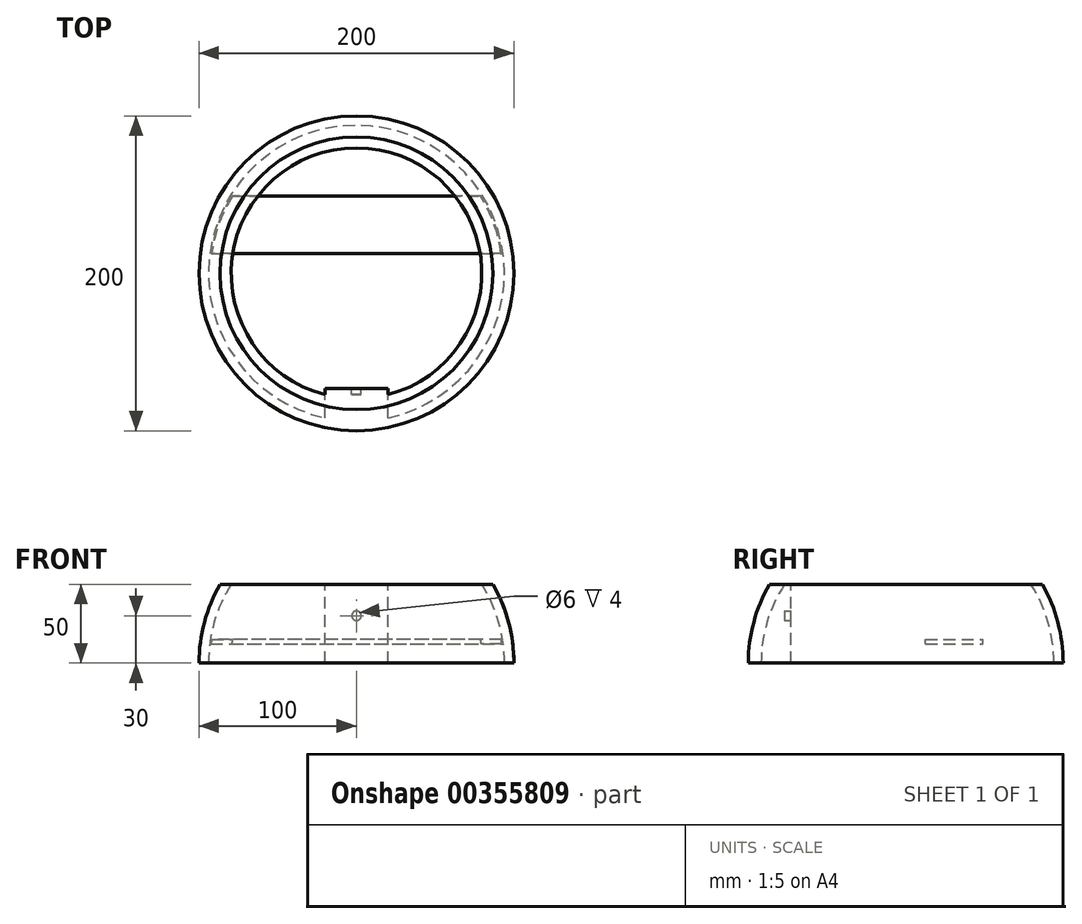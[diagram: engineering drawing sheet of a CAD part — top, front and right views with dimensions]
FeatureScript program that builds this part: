
annotation { "Feature Type Name" : "Feature", "Feature Type Description" : "" }
export const myFeature = defineFeature(function(context is Context, id is Id, definition is map)
    precondition{}
    {
        {
            var Q0;
            Q0=qCreatedBy(makeId("Front.planeOp"),FACE);
            var sketch = newSketch(context, id + "F0", { "sketchPlane" : qUnion([Q0])});
            skArc(sketch, "E0", {"start": v(-86.6, 50) * mm, "mid": v(-96.6, 25.88) * mm, "end": v(-100, 0) * mm});
            skLineSegment(sketch, "E1", {"start": v(0, 50) * mm, "end": v(0, 0) * mm});
            skLineSegment(sketch, "E2", {"start": v(0, 50) * mm, "end": v(-86.6, 50) * mm});
            skLineSegment(sketch, "E3", {"start": v(0, 0) * mm, "end": v(-100, 0) * mm});
            skPoint(sketch, "E4.orphan", {"position": v(0, 100) * mm});
            skSolve(sketch);
        }
        {
            var Q0;
            Q0=qSketchRegion(id+"F0",true);
            var Q1;
            Q1=sQuery(id+"F0.wireOp",EDGE,"E1");
            revolve(context, id + "F1", {"entities" : qUnion([Q0]), "axis" : qUnion([Q1]), "revolveType" : RevolveType.FULL});
        }
        {
            var Q0;
            Q0=makeQuery(id+"F1.opRevolve","SWEPT_FACE",FACE,{"disambiguationData":[OSD([sQuery(id+"F0.wireOp",EDGE,"E2")])]});
            var Q1;
            Q1=makeQuery(id+"F1.opRevolve","SWEPT_FACE",FACE,{"disambiguationData":[OSD([sQuery(id+"F0.wireOp",EDGE,"E3")])]});
            shell(context, id + "F2", {"entities" : qUnion([Q0, Q1]), "thickness" : 6 * mm});
        }
        {
            var Q0;
            Q0=qCreatedBy(makeId("Front.planeOp"),FACE);
            cPlane(context, id + "F3", {"entities" : qUnion([Q0]), "cplaneType" : CPlaneType.OFFSET, "offset" : 49 * mm, "oppositeDirection" : true, "width" : 150 * mm, "height" : 150 * mm});
        }
        {
            var Q0;
            Q0=qCreatedBy(id+"F3.planeOp",FACE);
            var sketch = newSketch(context, id + "F4", { "sketchPlane" : qUnion([Q0])});
            skLineSegment(sketch, "E5", {"start": v(47.2, 15) * mm, "end": v(-12.8, 15) * mm});
            skLineSegment(sketch, "E6", {"start": v(-12.8, 15) * mm, "end": v(-12.8, 12) * mm});
            skLineSegment(sketch, "E7", {"start": v(-12.8, 12) * mm, "end": v(47.2, 12) * mm});
            skLineSegment(sketch, "E8", {"start": v(47.2, 12) * mm, "end": v(47.2, 15) * mm});
            skSolve(sketch);
        }
        {
            var Q0;
            Q0=qSketchRegion(id+"F4",true);
            extrude(context, id + "F5", {"entities" : qUnion([Q0]), "depth" : 36.5 * mm});
        }
        {
            var Q0;
            Q0=makeQuery(id+"F5.opExtrude","SWEPT_FACE",FACE,{"disambiguationData":[OSD([sQuery(id+"F4.wireOp",EDGE,"E8")])]});
            extrude(context, id + "F6", {"entities" : qUnion([Q0]), "operationType" : NewBodyOperationType.ADD, "endBound" : BoundingType.UP_TO_NEXT, "depth" : 25 * mm});
        }
        {
            var Q0;
            Q0=makeQuery(id+"F5.opExtrude","SWEPT_FACE",FACE,{"disambiguationData":[OSD([sQuery(id+"F4.wireOp",EDGE,"E6")])]});
            extrude(context, id + "F7", {"entities" : qUnion([Q0]), "operationType" : NewBodyOperationType.ADD, "endBound" : BoundingType.UP_TO_NEXT, "depth" : 25 * mm});
        }
        {
            var Q0;
            Q0=qCreatedBy(makeId("Front.planeOp"),FACE);
            cPlane(context, id + "F8", {"entities" : qUnion([Q0]), "cplaneType" : CPlaneType.OFFSET, "offset" : 62 * mm, "width" : 150 * mm, "height" : 150 * mm});
        }
        {
            var Q0;
            Q0=qCreatedBy(id+"F8.planeOp",FACE);
            var sketch = newSketch(context, id + "F9", { "sketchPlane" : qUnion([Q0])});
            skLineSegment(sketch, "E9", {"start": v(20, 0) * mm, "end": v(20, 50) * mm});
            skLineSegment(sketch, "E10", {"start": v(-20, 0) * mm, "end": v(-20, 50) * mm});
            skLineSegment(sketch, "E11.0", {"start": v(-20, 0) * mm, "end": v(20, 0) * mm});
            skLineSegment(sketch, "E12.0", {"start": v(-20, 50) * mm, "end": v(20, 50) * mm});
            skPoint(sketch, "E13.orphan", {"position": v(-100, 0) * mm});
            skPoint(sketch, "E14.orphan", {"position": v(-86.6, 50) * mm});
            skPoint(sketch, "E15.orphan", {"position": v(100, 0) * mm});
            skPoint(sketch, "E16.orphan", {"position": v(86.6, 50) * mm});
            skSolve(sketch);
        }
        {
            var Q0;
            Q0=qSketchRegion(id+"F9",true);
            extrude(context, id + "F10", {"entities" : qUnion([Q0]), "operationType" : NewBodyOperationType.ADD, "endBound" : BoundingType.UP_TO_NEXT, "depth" : 25 * mm});
        }
        {
            var Q0;
            Q0=makeQuery(id+"F10.opExtrude","CAP_FACE",FACE,{"disambiguationData":[OSD([sQuery(id+"F9.wireOp",EDGE,"E9"),sQuery(id+"F9.wireOp",EDGE,"E10"),sQuery(id+"F9.wireOp",EDGE,"E11.0"),sQuery(id+"F9.wireOp",EDGE,"E12.0")])],"isStart":true});
            var sketch = newSketch(context, id + "F11", { "sketchPlane" : qUnion([Q0])});
            skCircle(sketch, "E17", {"center": v(0, 30) * mm, "radius": 3 * mm});
            skSolve(sketch);
        }
        {
            var Q0;
            Q0=makeQuery(id+"F11.imprint","IMPRINT",FACE,{"disambiguationData":[TD([[makeQuery(id+"F11.imprint","IMPRINT",EDGE,{"derivedFrom":sQuery(id+"F11.wireOp",EDGE,"E17")}),1.0]])]});
            extrude(context, id + "F12", {"entities" : qUnion([Q0]), "operationType" : NewBodyOperationType.REMOVE, "oppositeDirection" : true, "depth" : 4 * mm});
        }
        {
            var Q0;
            Q0=makeQuery(id+"F10.opExtrude","CAP_FACE",FACE,{"disambiguationData":[OSD([sQuery(id+"F9.wireOp",EDGE,"E9"),sQuery(id+"F9.wireOp",EDGE,"E10"),sQuery(id+"F9.wireOp",EDGE,"E11.0"),sQuery(id+"F9.wireOp",EDGE,"E12.0")])],"isStart":true});
            extrude(context, id + "F13", {"entities" : qUnion([Q0]), "operationType" : NewBodyOperationType.REMOVE, "oppositeDirection" : true, "depth" : 11 * mm});
        }
        {
            var Q0;
            Q0=makeQuery(id+"F12.boolean.opBoolean","COPY",FACE,{"derivedFrom":makeQuery(id+"F12.opExtrude","CAP_FACE",FACE,{"disambiguationData":[OSD([sQuery(id+"F11.wireOp",EDGE,"E17")])],"isStart":false})});
            extrude(context, id + "F14", {"entities" : qUnion([Q0]), "operationType" : NewBodyOperationType.REMOVE, "oppositeDirection" : true, "depth" : 11 * mm});
        }
    });
